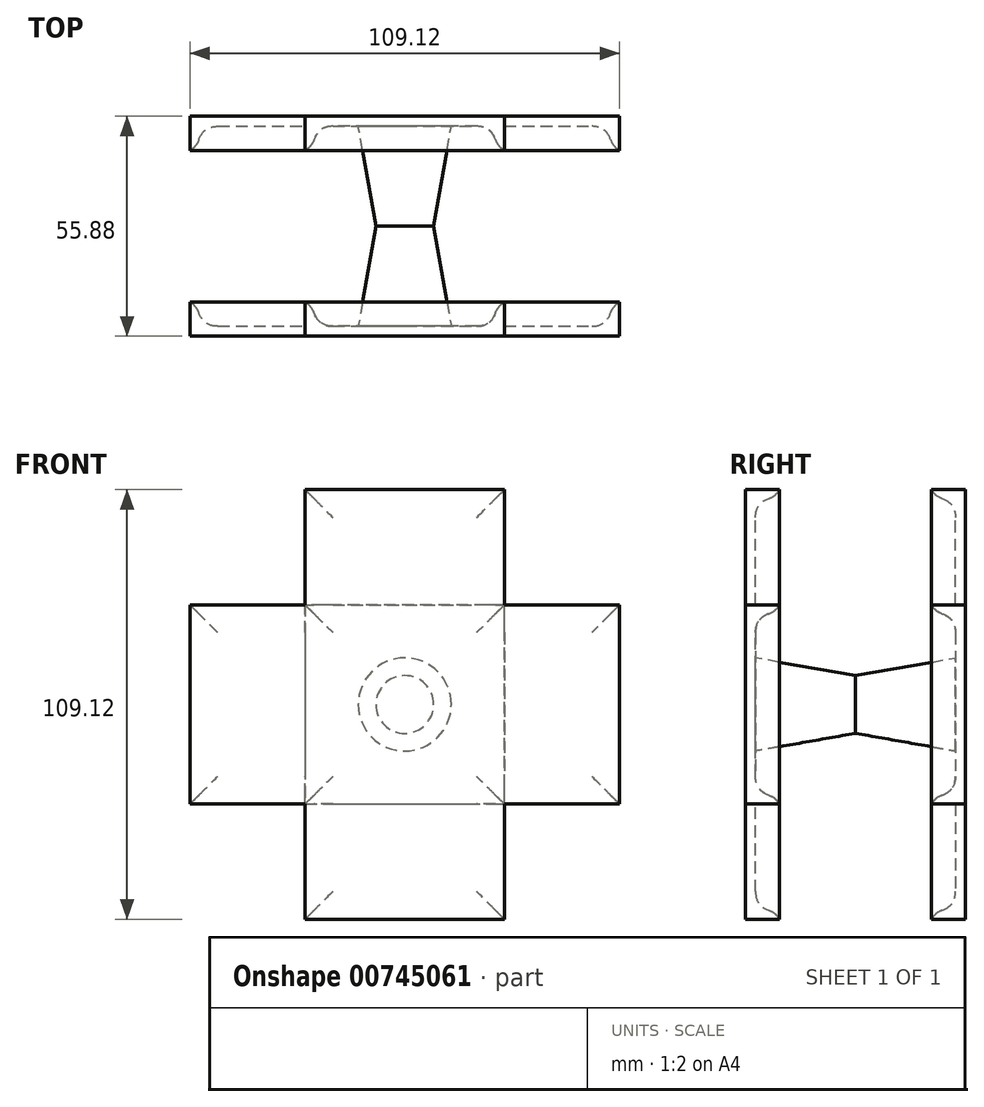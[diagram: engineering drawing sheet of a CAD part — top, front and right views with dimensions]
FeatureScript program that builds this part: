
annotation { "Feature Type Name" : "Feature", "Feature Type Description" : "" }
export const myFeature = defineFeature(function(context is Context, id is Id, definition is map)
    precondition{}
    {
        {
            var Q0;
            Q0=qCreatedBy(makeId("Front.planeOp"),FACE);
            var sketch = newSketch(context, id + "F0", { "sketchPlane" : qUnion([Q0])});
            skLineSegment(sketch, "E0.bottom", {"start": v(54.56, 25.3) * mm, "end": v(-54.56, 25.3) * mm});
            skLineSegment(sketch, "E0.top", {"start": v(54.56, -25.3) * mm, "end": v(-54.56, -25.3) * mm});
            skLineSegment(sketch, "E0.left", {"start": v(54.56, 25.3) * mm, "end": v(54.56, -25.3) * mm});
            skLineSegment(sketch, "E0.right", {"start": v(-54.56, 25.3) * mm, "end": v(-54.56, -25.3) * mm});
            skPoint(sketch, "E0.middle", {"position": v(0, 0) * mm});
            skSolve(sketch);
        }
        {
            var Q0;
            Q0=makeQuery(id+"F0.imprint","IMPRINT",FACE,{"disambiguationData":[TD([[makeQuery(id+"F0.imprint","IMPRINT",EDGE,{"derivedFrom":sQuery(id+"F0.wireOp",EDGE,"E0.bottom")}),1.0]])]});
            var Q1;
            Q1=sQuery(id+"F0.wireOp",EDGE,"E0.top");
            var Q2;
            Q2=sQuery(id+"F0.wireOp",EDGE,"E0.left");
            var Q3;
            Q3=sQuery(id+"F0.wireOp",EDGE,"E0.bottom");
            var Q4;
            Q4=sQuery(id+"F0.wireOp",EDGE,"E0.right");
            extrude(context, id + "F1", {"entities" : qUnion([Q0]), "surfaceEntities" : qUnion([Q1, Q2, Q3, Q4]), "depth" : 9.35 * mm, "offsetDistance" : 25.4 * mm});
        }
        {
            var Q0;
            Q0=makeQuery(id+"F1.opExtrude","CAP_FACE",FACE,{"disambiguationData":[OSD([sQuery(id+"F0.wireOp",EDGE,"E0.bottom"),sQuery(id+"F0.wireOp",EDGE,"E0.top"),sQuery(id+"F0.wireOp",EDGE,"E0.left"),sQuery(id+"F0.wireOp",EDGE,"E0.right")])],"isStart":false});
            var Q1;
            Q1=makeQuery(id+"F1.opExtrude","SWEPT_BODY",BODY,{"disambiguationData":[OSD([sQuery(id+"F0.wireOp",EDGE,"E0.bottom"),sQuery(id+"F0.wireOp",EDGE,"E0.top"),sQuery(id+"F0.wireOp",EDGE,"E0.left"),sQuery(id+"F0.wireOp",EDGE,"E0.right")])]});
            shell(context, id + "F2", {"entities" : qUnion([Q0]), "parts" : qUnion([Q1]), "thickness" : 2.54 * mm});
        }
        {
            var Q0;
            Q0=makeQuery(id+"F2.opShell","OFFSET_FACE",FACE,{"disambiguationData":[OSD([sQuery(id+"F0.wireOp",EDGE,"E0.bottom"),sQuery(id+"F0.wireOp",EDGE,"E0.top"),sQuery(id+"F0.wireOp",EDGE,"E0.left"),sQuery(id+"F0.wireOp",EDGE,"E0.right")])]});
            var sketch = newSketch(context, id + "F3", { "sketchPlane" : qUnion([Q0])});
            skCircle(sketch, "E1", {"center": v(0, 0) * mm, "radius": 11.81 * mm});
            skSolve(sketch);
        }
        {
            var Q0;
            Q0=makeQuery(id+"F3.imprint","IMPRINT",FACE,{"disambiguationData":[TD([[makeQuery(id+"F3.imprint","IMPRINT",EDGE,{"derivedFrom":sQuery(id+"F3.wireOp",EDGE,"E1")}),1.0]])]});
            var Q1;
            Q1=sQuery(id+"F3.wireOp",EDGE,"E1");
            extrude(context, id + "F4", {"entities" : qUnion([Q0]), "operationType" : NewBodyOperationType.ADD, "surfaceOperationType" : NewSurfaceOperationType.ADD, "surfaceEntities" : qUnion([Q1]), "depth" : 25.4 * mm, "offsetDistance" : 25.4 * mm, "hasDraft" : true, "draftAngle" : 10 * degree, "draftPullDirection" : true});
        }
        {
            var Q0;
            {var subQ0=sQuery(id+"F0.wireOp",EDGE,"E0.left");Q0=makeQuery(id+"F2.opShell","OFFSET_EDGE",EDGE,{"disambiguationData":[OSD([subQ0]),TDD([makeQuery(id+"F1.opExtrude","CAP_EDGE",EDGE,{"disambiguationData":[OSD([subQ0])],"isStart":false})])]});}
            var Q1;
            {var subQ0=sQuery(id+"F0.wireOp",EDGE,"E0.bottom");Q1=makeQuery(id+"F2.opShell","OFFSET_EDGE",EDGE,{"disambiguationData":[OSD([subQ0]),TDD([makeQuery(id+"F1.opExtrude","CAP_EDGE",EDGE,{"disambiguationData":[OSD([subQ0])],"isStart":false})])]});}
            var Q2;
            {var subQ0=sQuery(id+"F0.wireOp",EDGE,"E0.right");Q2=makeQuery(id+"F2.opShell","OFFSET_EDGE",EDGE,{"disambiguationData":[OSD([subQ0]),TDD([makeQuery(id+"F1.opExtrude","CAP_EDGE",EDGE,{"disambiguationData":[OSD([subQ0])],"isStart":false})])]});}
            var Q3;
            {var subQ0=sQuery(id+"F0.wireOp",EDGE,"E0.top");Q3=makeQuery(id+"F2.opShell","OFFSET_EDGE",EDGE,{"disambiguationData":[OSD([subQ0]),TDD([makeQuery(id+"F1.opExtrude","CAP_EDGE",EDGE,{"disambiguationData":[OSD([subQ0])],"isStart":false})])]});}
            fillet(context, id + "F5", {"entities" : qUnion([Q0, Q1, Q2, Q3]), "radius" : 5.08 * mm, "tangentPropagation" : true, "allowEdgeOverflow" : false});
        }
        {
            var Q0;
            {var subQ0=sQuery(id+"F0.wireOp",EDGE,"E0.right");Q0=makeQuery(id+"F2.opShell","OFFSET_EDGE",EDGE,{"disambiguationData":[OSD([subQ0]),TDD([makeQuery(id+"F1.opExtrude","CAP_EDGE",EDGE,{"disambiguationData":[OSD([subQ0])],"isStart":true})])]});}
            var Q1;
            {var subQ0=sQuery(id+"F0.wireOp",EDGE,"E0.bottom");Q1=makeQuery(id+"F2.opShell","OFFSET_EDGE",EDGE,{"disambiguationData":[OSD([subQ0]),TDD([makeQuery(id+"F1.opExtrude","CAP_EDGE",EDGE,{"disambiguationData":[OSD([subQ0])],"isStart":true})])]});}
            var Q2;
            {var subQ0=sQuery(id+"F0.wireOp",EDGE,"E0.left");Q2=makeQuery(id+"F2.opShell","OFFSET_EDGE",EDGE,{"disambiguationData":[OSD([subQ0]),TDD([makeQuery(id+"F1.opExtrude","CAP_EDGE",EDGE,{"disambiguationData":[OSD([subQ0])],"isStart":true})])]});}
            var Q3;
            {var subQ0=sQuery(id+"F0.wireOp",EDGE,"E0.top");Q3=makeQuery(id+"F2.opShell","OFFSET_EDGE",EDGE,{"disambiguationData":[OSD([subQ0]),TDD([makeQuery(id+"F1.opExtrude","CAP_EDGE",EDGE,{"disambiguationData":[OSD([subQ0])],"isStart":true})])]});}
            fillet(context, id + "F6", {"entities" : qUnion([Q0, Q1, Q2, Q3]), "radius" : 5.08 * mm, "tangentPropagation" : true, "rho" : 0.5, "crossSection" : FilletCrossSection.CONIC, "allowEdgeOverflow" : false});
        }
        {
            var Q0;
            Q0=makeQuery(id+"F1.opExtrude","SWEPT_BODY",BODY,{"disambiguationData":[OSD([sQuery(id+"F0.wireOp",EDGE,"E0.bottom"),sQuery(id+"F0.wireOp",EDGE,"E0.top"),sQuery(id+"F0.wireOp",EDGE,"E0.left"),sQuery(id+"F0.wireOp",EDGE,"E0.right")])]});
            var Q1;
            Q1=makeQuery(id+"F4.opExtrude","CAP_EDGE",EDGE,{"disambiguationData":[OSD([sQuery(id+"F3.wireOp",EDGE,"E1")])],"isStart":false});
            circularPattern(context, id + "F7", {"operationType" : NewBodyOperationType.ADD, "entities" : qUnion([Q0]), "axis" : qUnion([Q1]), "angle" : 360 * degree, "instanceCount" : 4, "equalSpace" : true});
        }
        {
            var Q0;
            Q0=makeQuery(id+"F1.opExtrude","SWEPT_BODY",BODY,{"disambiguationData":[OSD([sQuery(id+"F0.wireOp",EDGE,"E0.bottom"),sQuery(id+"F0.wireOp",EDGE,"E0.top"),sQuery(id+"F0.wireOp",EDGE,"E0.left"),sQuery(id+"F0.wireOp",EDGE,"E0.right")])]});
            var Q1;
            Q1=makeQuery(id+"F4.opExtrude","CAP_FACE",FACE,{"disambiguationData":[OSD([sQuery(id+"F3.wireOp",EDGE,"E1")])],"isStart":false});
            mirror(context, id + "F8", {"operationType" : NewBodyOperationType.ADD, "entities" : qUnion([Q0]), "mirrorPlane" : qUnion([Q1])});
        }
    });
